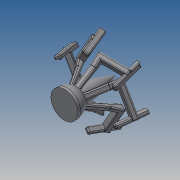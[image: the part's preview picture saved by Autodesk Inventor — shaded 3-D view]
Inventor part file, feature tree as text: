
AUTODESK INVENTOR PART (.ipt)
format: ipt  version: 2015 (Build 190159000, 159)  size: 592,384 bytes
history: native  units: mm
features: sketch x5, extrude x3, revolve x2, projected_geometry x2, fillet x1, pattern_circular x1
ambient origin geometry x8: Origin, YZ Plane, XZ Plane, XY Plane, X Axis, Y Axis, Z Axis, Center Point
bodies: Solid1 (feature_tree)
feature tree (14):
  revolve  "Revolution1"  [1 undecoded]
  extrude  "Extrusion1"  Depth=10.0mm TaperAngle=0.0deg
  extrude  "Extrusion2"  Depth=50.0mm TaperAngle=0.0deg
  extrude  "Extrusion3"  Depth=2.0mm
  fillet  "Fillet1"  Radius=15.0mm
  pattern_circular  "Circular Pattern1"  Count=20  [1 undecoded]
  revolve  "Revolution2"  Angle=90.0deg
  sketch  "Sketch1"  dims[d0=30.0mm d1=50.0mm]
  sketch  "Sketch2"  dims[d3=90.0deg d4=10.0mm d5=0.0mm]
  sketch  "Sketch3"  dims[d6=50.0mm d7=0.0mm d8=50.0mm d9=0.0mm]
  projected_geometry  "Projected Loop1"
  sketch  "Sketch4"  dims[d10=60.0mm d11=360.0deg d14=2.0mm d17=15.0mm]
  projected_geometry  "Projected Loop2"
  sketch  "Sketch5"  dims[d18=95.0mm d19=200.0mm d20=90.0deg]
note: 2 required parameter values undecoded (feature->parameter linkage not recoverable at this tier; creation-order binding heuristic only, values carry confidence <= 0.55)